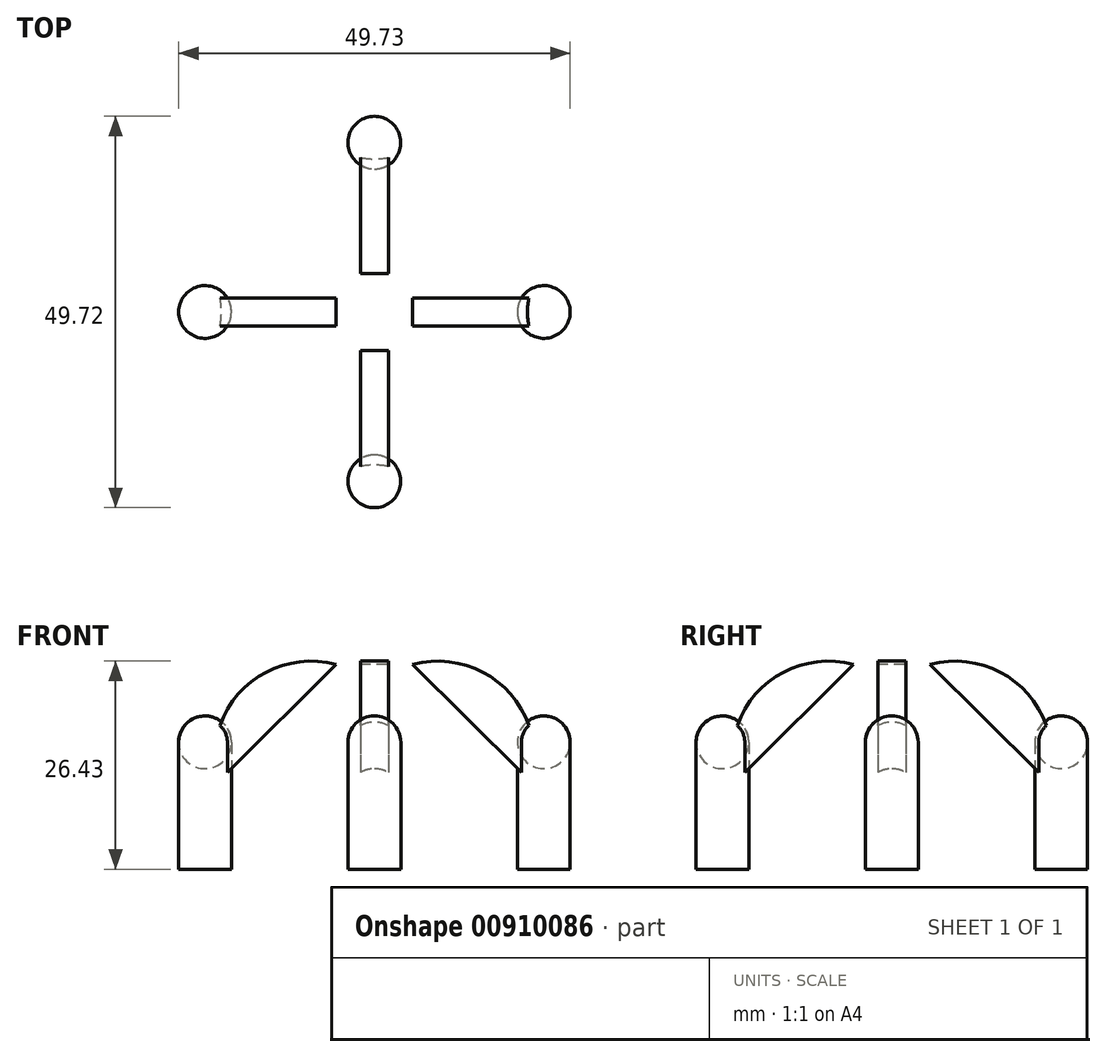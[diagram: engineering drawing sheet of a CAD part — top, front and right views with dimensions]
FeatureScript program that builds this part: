
annotation { "Feature Type Name" : "Feature", "Feature Type Description" : "" }
export const myFeature = defineFeature(function(context is Context, id is Id, definition is map)
    precondition{}
    {
        {
            var Q0;
            Q0=qCreatedBy(makeId("Front.planeOp"),FACE);
            var sketch = newSketch(context, id + "F0", { "sketchPlane" : qUnion([Q0])});
            skLineSegment(sketch, "E0", {"start": v(-29.5, 4.46) * mm, "end": v(-29.5, -40.44) * mm});
            skLineSegment(sketch, "E1", {"start": v(-10.35, -40.44) * mm, "end": v(-10.35, 4.46) * mm});
            skLineSegment(sketch, "E2", {"start": v(-29.5, 4.46) * mm, "end": v(-29.5, 32.75) * mm});
            skLineSegment(sketch, "E3", {"start": v(-10.35, 4.46) * mm, "end": v(-10.35, 32.75) * mm});
            skLineSegment(sketch, "E4", {"start": v(-29.5, 32.75) * mm, "end": v(-19.92, 41.1) * mm});
            skLineSegment(sketch, "E5", {"start": v(-10.35, 32.75) * mm, "end": v(-19.92, 41.1) * mm});
            skLineSegment(sketch, "E6", {"start": v(-44.79, -24.32) * mm, "end": v(-44.79, -40.44) * mm});
            skLineSegment(sketch, "E7", {"start": v(-38.09, -40.44) * mm, "end": v(-38.09, -24.32) * mm});
            skLineSegment(sketch, "E8", {"start": v(4.94, -24.32) * mm, "end": v(4.94, -40.44) * mm});
            skLineSegment(sketch, "E9", {"start": v(-44.79, -40.44) * mm, "end": v(-38.09, -40.44) * mm});
            skLineSegment(sketch, "E10", {"start": v(4.94, -40.44) * mm, "end": v(-1.76, -40.44) * mm});
            skLineSegment(sketch, "E11", {"start": v(-1.76, -40.44) * mm, "end": v(-1.76, -24.32) * mm});
            skLineSegment(sketch, "E12", {"start": v(-19.92, 53.32) * mm, "end": v(-19.92, -57.95) * mm});
            skPoint(sketch, "E12.endSnap0", {"position": v(-19.92, -30.02) * mm});
            skLineSegment(sketch, "E13", {"start": v(1.59, -53.1) * mm, "end": v(1.59, 13.65) * mm});
            skLineSegment(sketch, "E14", {"start": v(-41.44, -54.08) * mm, "end": v(-41.44, 14.64) * mm});
            skLineSegment(sketch, "E15", {"start": v(-44.79, -24.32) * mm, "end": v(-38.09, -24.32) * mm});
            skLineSegment(sketch, "E16", {"start": v(-1.76, -24.32) * mm, "end": v(4.94, -24.32) * mm});
            skLineSegment(sketch, "E17", {"start": v(-29.5, -40.44) * mm, "end": v(-10.35, -40.44) * mm});
            skArc(sketch, "E18", {"start": v(-38.09, -24.32) * mm, "mid": v(-41.44, -20.97) * mm, "end": v(-44.79, -24.32) * mm});
            skArc(sketch, "E19", {"start": v(4.94, -24.32) * mm, "mid": v(1.59, -20.97) * mm, "end": v(-1.76, -24.32) * mm});
            skSolve(sketch);
        }
        {
            var Q0;
            {var subQ1=sQuery(id+"F0.wireOp",EDGE,"NYmE5X03-ZxNv-JS0J-KoLE-2NSfzIN830l8");Q0=makeQuery(id+"F0.imprint","IMPRINT",FACE,{"disambiguationData":[TD([[makeQuery(id+"F0.imprint","IMPRINT",EDGE,{"derivedFrom":subQ1}),1.0]])]});}
            var Q1;
            {var subQ3=sQuery(id+"F0.wireOp",EDGE,"2jDveQg3-UYY0-kzGP-fbh1-aMBSOKZvZHeh");Q1=makeQuery(id+"F0.imprint","IMPRINT",FACE,{"disambiguationData":[TD([[makeQuery(id+"F0.imprint","IMPRINT",EDGE,{"derivedFrom":subQ3}),1.0]])]});}
            var Q2;
            Q2=sQuery(id+"F0.wireOp",EDGE,"E0");
            var Q3;
            Q3=sQuery(id+"F0.wireOp",EDGE,"E2");
            var Q4;
            Q4=sQuery(id+"F0.wireOp",EDGE,"E4");
            var Q5;
            Q5=sQuery(id+"F0.wireOp",EDGE,"2jDveQg3-UYY0-kzGP-fbh1-aMBSOKZvZHeh");
            var Q6;
            Q6=sQuery(id+"F0.wireOp",EDGE,"E12");
            revolve(context, id + "F1", {"bodyType" : ToolBodyType.SURFACE, "surfaceOperationType" : NewSurfaceOperationType.NEW, "entities" : qUnion([Q0, Q1]), "surfaceEntities" : qUnion([Q2, Q3, Q4, Q5]), "axis" : qUnion([Q6]), "revolveType" : RevolveType.FULL});
        }
        {
            var Q0;
            {var subQ0=sQuery(id+"F0.wireOp",EDGE,"E8");Q0=makeQuery(id+"F0.imprint","IMPRINT",FACE,{"disambiguationData":[TD([[makeQuery(id+"F0.imprint","IMPRINT",EDGE,{"derivedFrom":subQ0}),-1.0]])]});}
            var Q1;
            {var subQ0=sQuery(id+"F0.wireOp",EDGE,"Aj5AnHbf-aiAf-9EEF-htg3-RxBsWp403pAl");var subQ3=sQuery(id+"F0.wireOp",EDGE,"E13");var subQ5=makeQuery(id+"F0.imprint","INTERSECT",VERTEX,{"derivedFrom":[subQ0,subQ3]});Q1=makeQuery(id+"F0.imprint","IMPRINT",FACE,{"disambiguationData":[TD([[makeQuery(id+"F0.imprint","IMPRINT",EDGE,{"disambiguationData":[TD([[subQ5,-1.0]])],"derivedFrom":subQ3}),-1.0]])]});}
            var Q2;
            Q2=sQuery(id+"F0.wireOp",EDGE,"E8");
            var Q3;
            Q3=sQuery(id+"F0.wireOp",EDGE,"E13");
            revolve(context, id + "F2", {"surfaceOperationType" : NewSurfaceOperationType.NEW, "entities" : qUnion([Q0, Q1]), "surfaceEntities" : qUnion([Q2]), "axis" : qUnion([Q3]), "revolveType" : RevolveType.FULL});
        }
        {
            var Q0;
            Q0=makeQuery(id+"F2.opRevolve","SWEPT_BODY",BODY,{"disambiguationData":[OSD([sQuery(id+"F0.wireOp",EDGE,"E8"),sQuery(id+"F0.wireOp",EDGE,"Aj5AnHbf-aiAf-9EEF-htg3-RxBsWp403pAl"),sQuery(id+"F0.wireOp",EDGE,"E13"),sQuery(id+"F0.wireOp",EDGE,"E16")])]});
            var Q1;
            Q1=sQuery(id+"F0.wireOp",EDGE,"E12");
            circularPattern(context, id + "F3", {"entities" : qUnion([Q0]), "axis" : qUnion([Q1]), "angle" : 360 * degree, "instanceCount" : 4, "equalSpace" : true});
        }
        {
            var Q0;
            Q0=makeQuery(id+"F1.opRevolve","SWEPT_EDGE",EDGE,{"disambiguationData":[OSD([sQuery(id+"F0.wireOp",VERTEX,"E4.start")])]});
            fillet(context, id + "F4", {"entities" : qUnion([Q0]), "radius" : 5.08 * mm, "tangentPropagation" : true, "allowEdgeOverflow" : false});
        }
        {
            var Q0;
            Q0=qCreatedBy(makeId("Front.planeOp"),FACE);
            var sketch = newSketch(context, id + "F5", { "sketchPlane" : qUnion([Q0])});
            skArc(sketch, "E20", {"start": v(0, -29.37) * mm, "mid": v(-3.22, -17.56) * mm, "end": v(-15.06, -14.43) * mm});
            skLineSegment(sketch, "E21", {"start": v(-15.06, -14.43) * mm, "end": v(0, -29.37) * mm});
            skSolve(sketch);
        }
        {
            var Q0;
            Q0=makeQuery(id+"F5.imprint","IMPRINT",FACE,{"disambiguationData":[TD([[makeQuery(id+"F5.imprint","IMPRINT",EDGE,{"derivedFrom":sQuery(id+"F5.wireOp",EDGE,"E20")}),1.0]])]});
            extrude(context, id + "F6", {"entities" : qUnion([Q0]), "operationType" : NewBodyOperationType.ADD, "depth" : 1.78 * mm, "offsetDistance" : 25.4 * mm, "hasSecondDirection" : true, "secondDirectionOppositeDirection" : true, "secondDirectionDepth" : 1.78 * mm});
        }
        {
            var Q0;
            Q0=makeQuery(id+"F2.opRevolve","SWEPT_BODY",BODY,{"disambiguationData":[OSD([sQuery(id+"F0.wireOp",EDGE,"E8"),sQuery(id+"F0.wireOp",EDGE,"E10"),sQuery(id+"F0.wireOp",EDGE,"E13"),sQuery(id+"F0.wireOp",EDGE,"E19")])]});
            var Q1;
            Q1=sQuery(id+"F0.wireOp",EDGE,"E12");
            circularPattern(context, id + "F7", {"entities" : qUnion([Q0]), "axis" : qUnion([Q1]), "angle" : 360 * degree, "instanceCount" : 4, "equalSpace" : true});
        }
    });
